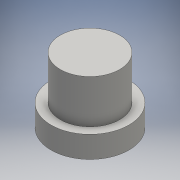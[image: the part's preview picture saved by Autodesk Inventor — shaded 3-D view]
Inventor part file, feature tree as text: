
AUTODESK INVENTOR PART (.ipt)
format: ipt  version: 2016 (Build 200138000, 138)  size: 96,768 bytes
history: native  units: mm
features: extrude x2, sketch x2
ambient origin geometry x8: Origin, YZ Plane, XZ Plane, XY Plane, X Axis, Y Axis, Z Axis, Center Point
bodies: Solid1 (feature_tree)
feature tree (4):
  extrude  "Extrusion1"  Depth=10.0mm TaperAngle=0.0deg
  extrude  "Extrusion2"  Depth=20.0mm TaperAngle=0.0deg
  sketch  "Sketch1"  dims[d0=35.75mm d1=10.0mm d2=0.0mm]
  sketch  "Sketch2"  dims[d3=27.3mm d4=20.0mm d5=0.0mm]
